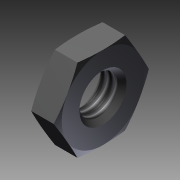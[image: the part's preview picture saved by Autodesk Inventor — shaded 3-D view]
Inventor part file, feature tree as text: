
AUTODESK INVENTOR PART (.ipt)
format: ipt  version: 2011 SP1 (Build 150282100, 282)  size: 120,320 bytes
history: native  units: mm
features: other x7, sketch x3, revolve x2, extrude x1, thread x1
ambient origin geometry x8: Origin, YZ Plane, XZ Plane, XY Plane, X Axis, Y Axis, Z Axis, Center Point
bodies: Solid1 (feature_tree)
feature tree (14):
  revolve  "Revolution1"  [1 undecoded]
  extrude  "Extrusion1"  Depth=1.442mm TaperAngle=0.0deg
  revolve  "Revolution2"  [1 undecoded]
  thread  "Thread1"  [1 undecoded]
  other  "M_XY"
  other  "M_YZ"
  other  "M_ZX"
  other  "M_X"
  other  "M_Y"
  other  "M_Z"
  other  "M_Center"
  sketch  "Skizze_1"  dims[d0=360.0deg d1=10.0mm d2=0.0mm]
  sketch  "Skizze_2"  dims[d3=360.0deg d4=1.442mm d5=0.0mm]
  sketch  "Skizze_3"
note: 3 required parameter values undecoded (feature->parameter linkage not recoverable at this tier; creation-order binding heuristic only, values carry confidence <= 0.55)